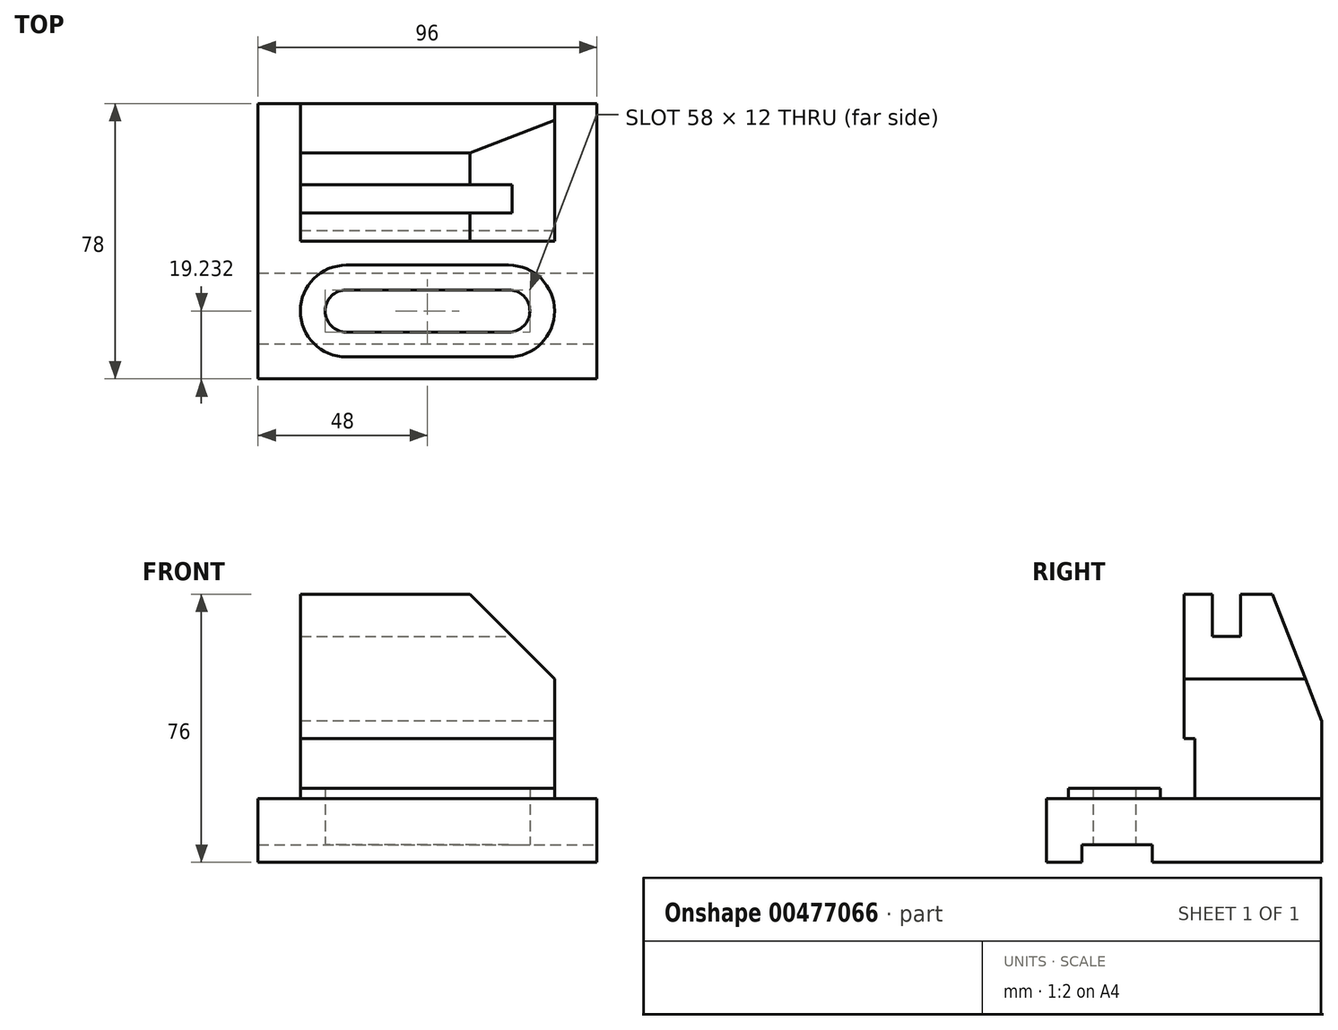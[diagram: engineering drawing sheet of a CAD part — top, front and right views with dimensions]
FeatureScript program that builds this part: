
annotation { "Feature Type Name" : "Feature", "Feature Type Description" : "" }
export const myFeature = defineFeature(function(context is Context, id is Id, definition is map)
    precondition{}
    {
        {
            var Q0;
            Q0=qCreatedBy(makeId("Top.planeOp"),FACE);
            var sketch = newSketch(context, id + "F0", { "sketchPlane" : qUnion([Q0])});
            skLineSegment(sketch, "E0.bottom", {"start": v(0, 0) * mm, "end": v(96, 0) * mm});
            skLineSegment(sketch, "E0.top", {"start": v(0, 78) * mm, "end": v(96, 78) * mm});
            skLineSegment(sketch, "E0.left", {"start": v(0, 0) * mm, "end": v(0, 78) * mm});
            skLineSegment(sketch, "E0.right", {"start": v(96, 0) * mm, "end": v(96, 78) * mm});
            skSolve(sketch);
        }
        {
            var Q0;
            Q0 = qSketchRegion(id + "F0", true);
            extrude(context, id + "F1", {"entities" : qUnion([Q0]), "depth" : 18 * mm});
        }
        {
            var Q0;
            Q0=makeQuery(id+"F1.opExtrude","CAP_FACE",FACE,{"disambiguationData":[OSD([sQuery(id+"F0.wireOp",EDGE,"E0.bottom"),sQuery(id+"F0.wireOp",EDGE,"E0.top"),sQuery(id+"F0.wireOp",EDGE,"E0.left"),sQuery(id+"F0.wireOp",EDGE,"E0.right")])],"isStart":false});
            var sketch = newSketch(context, id + "F2", { "sketchPlane" : qUnion([Q0])});
            skLineSegment(sketch, "E1.bottom", {"start": v(84, 78) * mm, "end": v(12, 78) * mm});
            skLineSegment(sketch, "E1.top", {"start": v(84, 39) * mm, "end": v(12, 39) * mm});
            skLineSegment(sketch, "E1.left", {"start": v(84, 78) * mm, "end": v(84, 39) * mm});
            skLineSegment(sketch, "E1.right", {"start": v(12, 78) * mm, "end": v(12, 39) * mm});
            skSolve(sketch);
        }
        {
            var Q0;
            Q0 = qSketchRegion(id + "F2", true);
            extrude(context, id + "F3", {"entities" : qUnion([Q0]), "operationType" : NewBodyOperationType.ADD, "depth" : 58 * mm});
        }
        {
            var Q0;
            Q0=makeQuery(id+"F3.opExtrude","CAP_FACE",FACE,{"disambiguationData":[OSD([sQuery(id+"F2.wireOp",EDGE,"E1.bottom"),sQuery(id+"F2.wireOp",EDGE,"E1.top"),sQuery(id+"F2.wireOp",EDGE,"E1.left"),sQuery(id+"F2.wireOp",EDGE,"E1.right")])],"isStart":false});
            var sketch = newSketch(context, id + "F4", { "sketchPlane" : qUnion([Q0])});
            skLineSegment(sketch, "E2.bottom", {"start": v(12, 55) * mm, "end": v(84, 55) * mm});
            skLineSegment(sketch, "E2.top", {"start": v(12, 47) * mm, "end": v(84, 47) * mm});
            skLineSegment(sketch, "E2.left", {"start": v(12, 55) * mm, "end": v(12, 47) * mm});
            skLineSegment(sketch, "E2.right", {"start": v(84, 55) * mm, "end": v(84, 47) * mm});
            skSolve(sketch);
        }
        {
            var Q0;
            Q0 = qSketchRegion(id + "F4", true);
            extrude(context, id + "F5", {"entities" : qUnion([Q0]), "operationType" : NewBodyOperationType.REMOVE, "oppositeDirection" : true, "depth" : 12 * mm});
        }
        {
            var Q0;
            Q0=makeQuery(id+"F1.opExtrude","CAP_FACE",FACE,{"disambiguationData":[OSD([sQuery(id+"F0.wireOp",EDGE,"E0.bottom"),sQuery(id+"F0.wireOp",EDGE,"E0.top"),sQuery(id+"F0.wireOp",EDGE,"E0.left"),sQuery(id+"F0.wireOp",EDGE,"E0.right")])],"isStart":true});
            var sketch = newSketch(context, id + "F6", { "sketchPlane" : qUnion([Q0])});
            skLineSegment(sketch, "E3.bottom", {"start": v(0, -30) * mm, "end": v(96, -30) * mm});
            skLineSegment(sketch, "E3.top", {"start": v(0, -10) * mm, "end": v(96, -10) * mm});
            skLineSegment(sketch, "E3.left", {"start": v(0, -30) * mm, "end": v(0, -10) * mm});
            skLineSegment(sketch, "E3.right", {"start": v(96, -30) * mm, "end": v(96, -10) * mm});
            skSolve(sketch);
        }
        {
            var Q0;
            Q0 = qSketchRegion(id + "F6", true);
            extrude(context, id + "F7", {"entities" : qUnion([Q0]), "operationType" : NewBodyOperationType.REMOVE, "oppositeDirection" : true, "depth" : 5 * mm});
        }
        {
            var Q0;
            Q0=makeQuery(id+"F3.boolean.opBoolean","MERGE",FACE,{"derivedFrom":[makeQuery(id+"F1.opExtrude","SWEPT_FACE",FACE,{"disambiguationData":[OSD([sQuery(id+"F0.wireOp",EDGE,"E0.top")])]}),makeQuery(id+"F3.opExtrude","SWEPT_FACE",FACE,{"disambiguationData":[OSD([sQuery(id+"F2.wireOp",EDGE,"E1.bottom")])]})]});
            var sketch = newSketch(context, id + "F8", { "sketchPlane" : qUnion([Q0])});
            skSolve(sketch);
        }
        {
            var Q0;
            Q0=makeQuery(id+"F3.opExtrude","SWEPT_FACE",FACE,{"disambiguationData":[OSD([sQuery(id+"F2.wireOp",EDGE,"E1.top")])]});
            var sketch = newSketch(context, id + "F9", { "sketchPlane" : qUnion([Q0])});
            skLineSegment(sketch, "E4", {"start": v(60, 76) * mm, "end": v(84, 52) * mm});
            skSolve(sketch);
        }
        {
            var Q0;
            {var subQ0=sQuery(id+"F9.wireOp",EDGE,"E4");Q0=makeQuery(id+"F9.imprint","IMPRINT",FACE,{"disambiguationData":[TD([[makeQuery(id+"F9.imprint","IMPRINT",EDGE,{"derivedFrom":subQ0}),1.0]])]});}
            var Q1;
            {var subQ2=sQuery(id+"F0.wireOp",EDGE,"E0.top");Q1=makeQuery(id+"F8.imprint","IMPRINT",FACE,{"disambiguationData":[TD([[makeQuery(id+"F8.imprint","IMPRINT",EDGE,{"derivedFrom":makeQuery(id+"F1.opExtrude","CAP_EDGE",EDGE,{"disambiguationData":[OSD([subQ2])],"isStart":true})}),-1.0]])]});}
            extrude(context, id + "F10", {"entities" : qUnion([Q0, Q1]), "operationType" : NewBodyOperationType.REMOVE, "endBound" : BoundingType.THROUGH_ALL, "oppositeDirection" : true, "depth" : 25 * mm});
        }
        {
            var Q0;
            Q0=makeQuery(id+"F1.opExtrude","CAP_FACE",FACE,{"disambiguationData":[OSD([sQuery(id+"F0.wireOp",EDGE,"E0.bottom"),sQuery(id+"F0.wireOp",EDGE,"E0.top"),sQuery(id+"F0.wireOp",EDGE,"E0.left"),sQuery(id+"F0.wireOp",EDGE,"E0.right")])],"isStart":false});
            var sketch = newSketch(context, id + "F11", { "sketchPlane" : qUnion([Q0])});
            skLineSegment(sketch, "E5", {"start": v(25, 19.23) * mm, "end": v(71, 19.23) * mm, "construction": true});
            skArc(sketch, "E6.0.startCap", {"start": v(25, 13.23) * mm, "mid": v(19, 19.23) * mm, "end": v(25, 25.23) * mm});
            skArc(sketch, "E6.0.endCap", {"start": v(71, 25.23) * mm, "mid": v(77, 19.23) * mm, "end": v(71, 13.23) * mm});
            skLineSegment(sketch, "E6.0.left", {"start": v(25, 25.23) * mm, "end": v(71, 25.23) * mm});
            skLineSegment(sketch, "E6.0.right", {"start": v(25, 13.23) * mm, "end": v(71, 13.23) * mm});
            skArc(sketch, "E7.0.startCap", {"start": v(25, 6.23) * mm, "mid": v(12, 19.23) * mm, "end": v(25, 32.23) * mm});
            skArc(sketch, "E7.0.endCap", {"start": v(71, 32.23) * mm, "mid": v(84, 19.23) * mm, "end": v(71, 6.23) * mm});
            skLineSegment(sketch, "E7.0.left", {"start": v(25, 32.23) * mm, "end": v(71, 32.23) * mm});
            skLineSegment(sketch, "E7.0.right", {"start": v(25, 6.23) * mm, "end": v(71, 6.23) * mm});
            skSolve(sketch);
        }
        {
            var Q0;
            Q0 = qSketchRegion(id + "F11", true);
            extrude(context, id + "F12", {"entities" : qUnion([Q0]), "operationType" : NewBodyOperationType.ADD, "depth" : 3 * mm});
        }
        {
            var Q0;
            Q0=makeQuery(id+"F12.boolean.opBoolean","SPLIT",FACE,{"disambiguationData":[TD([makeQuery(id+"F12.opExtrude","SWEPT_FACE",FACE,{"disambiguationData":[OSD([sQuery(id+"F11.wireOp",EDGE,"E6.0.startCap")])]})])],"derivedFrom":makeQuery(id+"F1.opExtrude","CAP_FACE",FACE,{"disambiguationData":[OSD([sQuery(id+"F0.wireOp",EDGE,"E0.bottom"),sQuery(id+"F0.wireOp",EDGE,"E0.top"),sQuery(id+"F0.wireOp",EDGE,"E0.left"),sQuery(id+"F0.wireOp",EDGE,"E0.right")])],"isStart":false})});
            extrude(context, id + "F13", {"entities" : qUnion([Q0]), "operationType" : NewBodyOperationType.REMOVE, "endBound" : BoundingType.THROUGH_ALL, "oppositeDirection" : true, "depth" : 25 * mm});
        }
        {
            var Q0;
            Q0=makeQuery(id+"F3.opExtrude","SWEPT_FACE",FACE,{"disambiguationData":[OSD([sQuery(id+"F2.wireOp",EDGE,"E1.right")])]});
            var sketch = newSketch(context, id + "F14", { "sketchPlane" : qUnion([Q0])});
            skLineSegment(sketch, "E8", {"start": v(-78, 76) * mm, "end": v(-64, 76) * mm});
            skLineSegment(sketch, "E9", {"start": v(-78, 76) * mm, "end": v(-78, 40) * mm});
            skLineSegment(sketch, "E10", {"start": v(-78, 40) * mm, "end": v(-64, 76) * mm});
            skSolve(sketch);
        }
        {
            var Q0;
            Q0 = qSketchRegion(id + "F14", true);
            extrude(context, id + "F15", {"entities" : qUnion([Q0]), "operationType" : NewBodyOperationType.REMOVE, "endBound" : BoundingType.THROUGH_ALL, "oppositeDirection" : true, "depth" : 25 * mm});
        }
        {
            var Q0;
            Q0=makeQuery(id+"F3.opExtrude","SWEPT_FACE",FACE,{"disambiguationData":[OSD([sQuery(id+"F2.wireOp",EDGE,"E1.top")])]});
            var sketch = newSketch(context, id + "F16", { "sketchPlane" : qUnion([Q0])});
            skLineSegment(sketch, "E11.bottom", {"start": v(12, 18) * mm, "end": v(84, 18) * mm});
            skLineSegment(sketch, "E11.top", {"start": v(12, 35) * mm, "end": v(84, 35) * mm});
            skLineSegment(sketch, "E11.left", {"start": v(12, 18) * mm, "end": v(12, 35) * mm});
            skLineSegment(sketch, "E11.right", {"start": v(84, 18) * mm, "end": v(84, 35) * mm});
            skSolve(sketch);
        }
        {
            var Q0;
            Q0 = qSketchRegion(id + "F16", true);
            extrude(context, id + "F17", {"entities" : qUnion([Q0]), "operationType" : NewBodyOperationType.REMOVE, "oppositeDirection" : true, "depth" : 3 * mm});
        }
    });
